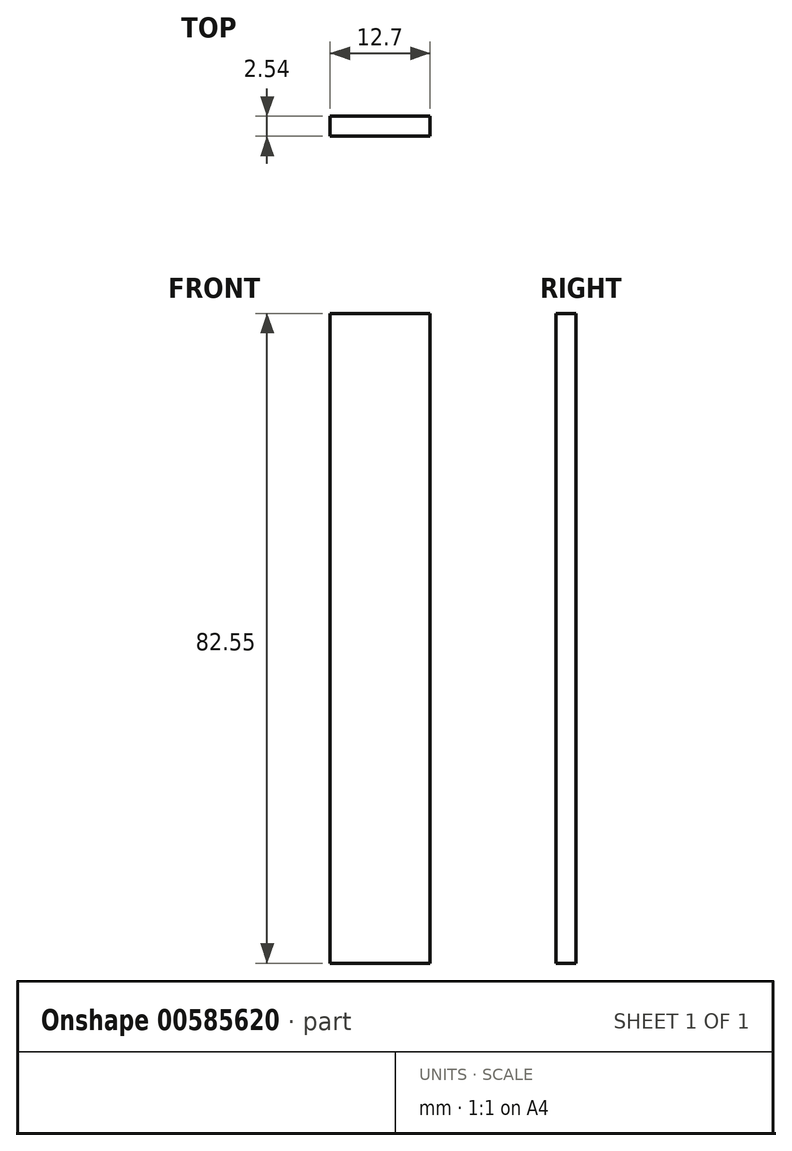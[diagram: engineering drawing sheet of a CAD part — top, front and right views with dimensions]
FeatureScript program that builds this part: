
annotation { "Feature Type Name" : "Feature", "Feature Type Description" : "" }
export const myFeature = defineFeature(function(context is Context, id is Id, definition is map)
    precondition{}
    {
        {
            var Q0;
            Q0=qCreatedBy(makeId("Top.planeOp"),FACE);
            var sketch = newSketch(context, id + "F0", { "sketchPlane" : qUnion([Q0])});
            skLineSegment(sketch, "E0.bottom", {"start": v(-6.35, 1.27) * mm, "end": v(6.35, 1.27) * mm});
            skLineSegment(sketch, "E0.top", {"start": v(-6.35, -1.27) * mm, "end": v(6.35, -1.27) * mm});
            skLineSegment(sketch, "E0.left", {"start": v(-6.35, 1.27) * mm, "end": v(-6.35, -1.27) * mm});
            skLineSegment(sketch, "E0.right", {"start": v(6.35, 1.27) * mm, "end": v(6.35, -1.27) * mm});
            skPoint(sketch, "E0.middle", {"position": v(0, 0) * mm});
            skSolve(sketch);
        }
        {
            var Q0;
            Q0=makeQuery(id+"F0.imprint","IMPRINT",FACE,{"disambiguationData":[TD([[makeQuery(id+"F0.imprint","IMPRINT",EDGE,{"derivedFrom":sQuery(id+"F0.wireOp",EDGE,"E0.bottom")}),-1.0]])]});
            extrude(context, id + "F1", {"entities" : qUnion([Q0]), "depth" : 82.55 * mm, "offsetDistance" : 25.4 * mm});
        }
    });
